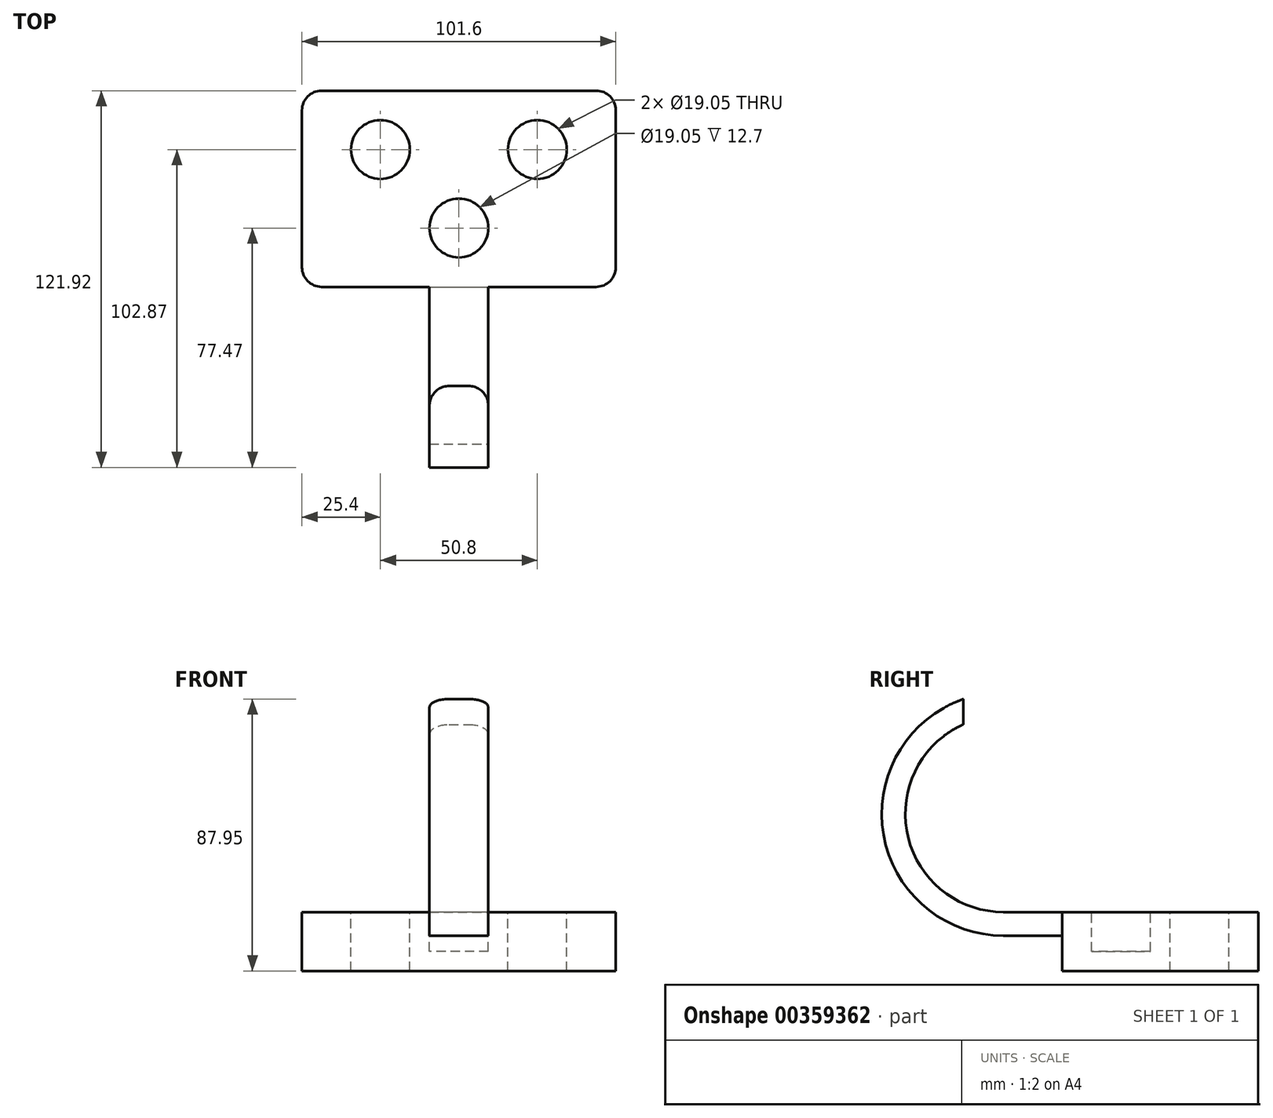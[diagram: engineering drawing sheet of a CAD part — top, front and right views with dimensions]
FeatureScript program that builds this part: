
annotation { "Feature Type Name" : "Feature", "Feature Type Description" : "" }
export const myFeature = defineFeature(function(context is Context, id is Id, definition is map)
    precondition{}
    {
        {
            var Q0;
            Q0=qCreatedBy(makeId("Top.planeOp"),FACE);
            var sketch = newSketch(context, id + "F0", { "sketchPlane" : qUnion([Q0])});
            skLineSegment(sketch, "E0", {"start": v(-50.8, 31.75) * mm, "end": v(-50.8, -31.75) * mm});
            skLineSegment(sketch, "E1", {"start": v(-50.8, -31.75) * mm, "end": v(50.8, -31.75) * mm});
            skLineSegment(sketch, "E2", {"start": v(50.8, -31.75) * mm, "end": v(50.8, 31.75) * mm});
            skLineSegment(sketch, "E3", {"start": v(50.8, 31.75) * mm, "end": v(-50.8, 31.75) * mm});
            skLineSegment(sketch, "E4", {"start": v(-50.8, 0) * mm, "end": v(50.8, 0) * mm});
            skLineSegment(sketch, "E5", {"start": v(0, 31.75) * mm, "end": v(0, -31.75) * mm});
            skCircle(sketch, "E6", {"center": v(-25.4, 12.7) * mm, "radius": 9.53 * mm});
            skCircle(sketch, "E7", {"center": v(25.4, 12.7) * mm, "radius": 9.53 * mm});
            skCircle(sketch, "E8", {"center": v(0, -12.7) * mm, "radius": 9.53 * mm});
            skLineSegment(sketch, "E9", {"start": v(-9.52, -31.75) * mm, "end": v(-9.52, -50.8) * mm});
            skLineSegment(sketch, "E10", {"start": v(-9.52, -50.8) * mm, "end": v(9.53, -50.8) * mm});
            skLineSegment(sketch, "E11", {"start": v(9.53, -50.8) * mm, "end": v(9.53, -31.75) * mm});
            skSolve(sketch);
        }
        {
            var Q0;
            {var subQ3=sQuery(id+"F0.wireOp",EDGE,"E5");var subQ5=sQuery(id+"F0.wireOp",EDGE,"E1");var subQ8=makeQuery(id+"F0.imprint","INTERSECT",VERTEX,{"derivedFrom":[subQ5,subQ3]});Q0=makeQuery(id+"F0.imprint","IMPRINT",FACE,{"disambiguationData":[TD([[makeQuery(id+"F0.imprint","IMPRINT",EDGE,{"disambiguationData":[TD([[subQ8,-1.0]])],"derivedFrom":subQ5}),1.0]])]});}
            var Q1;
            {var subQ0=sQuery(id+"F0.wireOp",EDGE,"E8");var subQ1=sQuery(id+"F0.wireOp",EDGE,"E5");var subQ2=makeQuery(id+"F0.imprint","INTERSECT",VERTEX,{"disambiguationData":[OD(0.0)],"derivedFrom":[subQ1,subQ0]});Q1=makeQuery(id+"F0.imprint","IMPRINT",FACE,{"disambiguationData":[TD([[makeQuery(id+"F0.imprint","IMPRINT",EDGE,{"disambiguationData":[TD([[subQ2,-1.0]])],"derivedFrom":subQ1}),-1.0]])]});}
            var Q2;
            {var subQ1=sQuery(id+"F0.wireOp",EDGE,"E0");var subQ5=sQuery(id+"F0.wireOp",EDGE,"E1");var subQ8=makeQuery(id+"F0.imprint","INTERSECT",VERTEX,{"derivedFrom":[subQ1,subQ5]});Q2=makeQuery(id+"F0.imprint","IMPRINT",FACE,{"disambiguationData":[TD([[makeQuery(id+"F0.imprint","IMPRINT",EDGE,{"disambiguationData":[TD([[subQ8,1.0]])],"derivedFrom":subQ1}),1.0]])]});}
            var Q3;
            {var subQ0=sQuery(id+"F0.wireOp",EDGE,"E8");var subQ1=sQuery(id+"F0.wireOp",EDGE,"E5");var subQ2=makeQuery(id+"F0.imprint","INTERSECT",VERTEX,{"disambiguationData":[OD(0.0)],"derivedFrom":[subQ1,subQ0]});Q3=makeQuery(id+"F0.imprint","IMPRINT",FACE,{"disambiguationData":[TD([[makeQuery(id+"F0.imprint","IMPRINT",EDGE,{"disambiguationData":[TD([[subQ2,-1.0]])],"derivedFrom":subQ1}),1.0]])]});}
            var Q4;
            Q4=makeQuery(id+"F0.imprint","IMPRINT",FACE,{"disambiguationData":[TD([[makeQuery(id+"F0.imprint","IMPRINT",EDGE,{"derivedFrom":sQuery(id+"F0.wireOp",EDGE,"E6")}),1.0]])]});
            var Q5;
            Q5=makeQuery(id+"F0.imprint","IMPRINT",FACE,{"disambiguationData":[TD([[makeQuery(id+"F0.imprint","IMPRINT",EDGE,{"derivedFrom":sQuery(id+"F0.wireOp",EDGE,"E6")}),-1.0]])]});
            var Q6;
            Q6=makeQuery(id+"F0.imprint","IMPRINT",FACE,{"disambiguationData":[TD([[makeQuery(id+"F0.imprint","IMPRINT",EDGE,{"derivedFrom":sQuery(id+"F0.wireOp",EDGE,"E7")}),-1.0]])]});
            var Q7;
            Q7=makeQuery(id+"F0.imprint","IMPRINT",FACE,{"disambiguationData":[TD([[makeQuery(id+"F0.imprint","IMPRINT",EDGE,{"derivedFrom":sQuery(id+"F0.wireOp",EDGE,"E7")}),1.0]])]});
            extrude(context, id + "F1", {"entities" : qUnion([Q0, Q1, Q2, Q3, Q4, Q5, Q6, Q7]), "oppositeDirection" : true, "depth" : 19.05 * mm});
        }
        {
            var Q0;
            {var subQ0=sQuery(id+"F0.wireOp",EDGE,"E9");Q0=makeQuery(id+"F0.imprint","IMPRINT",FACE,{"disambiguationData":[TD([[makeQuery(id+"F0.imprint","IMPRINT",EDGE,{"derivedFrom":subQ0}),1.0]])]});}
            extrude(context, id + "F2", {"entities" : qUnion([Q0]), "operationType" : NewBodyOperationType.ADD, "oppositeDirection" : true, "depth" : 7.62 * mm});
        }
        {
            var Q0;
            Q0=makeQuery(id+"F0.imprint","IMPRINT",FACE,{"disambiguationData":[TD([[makeQuery(id+"F0.imprint","IMPRINT",EDGE,{"derivedFrom":sQuery(id+"F0.wireOp",EDGE,"E6")}),1.0]])]});
            extrude(context, id + "F3", {"entities" : qUnion([Q0]), "operationType" : NewBodyOperationType.REMOVE, "endBound" : BoundingType.THROUGH_ALL, "oppositeDirection" : true, "depth" : 25.4 * mm});
        }
        {
            var Q0;
            {var subQ0=sQuery(id+"F0.wireOp",EDGE,"E8");var subQ1=sQuery(id+"F0.wireOp",EDGE,"E5");var subQ2=makeQuery(id+"F0.imprint","INTERSECT",VERTEX,{"disambiguationData":[OD(0.0)],"derivedFrom":[subQ1,subQ0]});Q0=makeQuery(id+"F0.imprint","IMPRINT",FACE,{"disambiguationData":[TD([[makeQuery(id+"F0.imprint","IMPRINT",EDGE,{"disambiguationData":[TD([[subQ2,-1.0]])],"derivedFrom":subQ1}),-1.0]])]});}
            var Q1;
            {var subQ0=sQuery(id+"F0.wireOp",EDGE,"E8");var subQ1=sQuery(id+"F0.wireOp",EDGE,"E5");var subQ2=makeQuery(id+"F0.imprint","INTERSECT",VERTEX,{"disambiguationData":[OD(0.0)],"derivedFrom":[subQ1,subQ0]});Q1=makeQuery(id+"F0.imprint","IMPRINT",FACE,{"disambiguationData":[TD([[makeQuery(id+"F0.imprint","IMPRINT",EDGE,{"disambiguationData":[TD([[subQ2,-1.0]])],"derivedFrom":subQ1}),1.0]])]});}
            extrude(context, id + "F4", {"entities" : qUnion([Q0, Q1]), "operationType" : NewBodyOperationType.REMOVE, "oppositeDirection" : true, "depth" : 12.7 * mm});
        }
        {
            var Q0;
            Q0=makeQuery(id+"F1.opExtrude","SWEPT_EDGE",EDGE,{"disambiguationData":[OSD([sQuery(id+"F0.wireOp",EDGE,"E0"),sQuery(id+"F0.wireOp",EDGE,"E3")])]});
            var Q1;
            Q1=makeQuery(id+"F1.opExtrude","SWEPT_EDGE",EDGE,{"disambiguationData":[OSD([sQuery(id+"F0.wireOp",EDGE,"E0"),sQuery(id+"F0.wireOp",EDGE,"E1")])]});
            var Q2;
            Q2=makeQuery(id+"F1.opExtrude","SWEPT_EDGE",EDGE,{"disambiguationData":[OSD([sQuery(id+"F0.wireOp",EDGE,"E2"),sQuery(id+"F0.wireOp",EDGE,"E3")])]});
            var Q3;
            Q3=makeQuery(id+"F1.opExtrude","SWEPT_EDGE",EDGE,{"disambiguationData":[OSD([sQuery(id+"F0.wireOp",EDGE,"E1"),sQuery(id+"F0.wireOp",EDGE,"E2")])]});
            fillet(context, id + "F5", {"entities" : qUnion([Q0, Q1, Q2, Q3]), "radius" : 6.35 * mm, "tangentPropagation" : true, "allowEdgeOverflow" : false});
        }
        {
            var Q0;
            Q0=makeQuery(id+"F2.opExtrude","SWEPT_FACE",FACE,{"disambiguationData":[OSD([sQuery(id+"F0.wireOp",EDGE,"E11")])]});
            var sketch = newSketch(context, id + "F6", { "sketchPlane" : qUnion([Q0])});
            skLineSegment(sketch, "E12.0.0", {"start": v(-31.75, 0) * mm, "end": v(-50.8, 0) * mm});
            skLineSegment(sketch, "E12.0.1", {"start": v(-50.8, 0) * mm, "end": v(-50.8, -7.62) * mm});
            skLineSegment(sketch, "E12.0.2", {"start": v(-50.8, -7.62) * mm, "end": v(-31.75, -7.62) * mm});
            skLineSegment(sketch, "E12.0.3", {"start": v(-31.75, -7.62) * mm, "end": v(-31.75, 0) * mm});
            skArc(sketch, "E13", {"start": v(-50.8, -7.62) * mm, "mid": v(-89.61, 25.14) * mm, "end": v(-63.83, 68.9) * mm});
            skLineSegment(sketch, "E14", {"start": v(-63.83, 68.9) * mm, "end": v(-63.83, 60.7) * mm});
            skLineSegment(sketch, "E15", {"start": v(-31.75, -7.62) * mm, "end": v(-31.75, 116.77) * mm});
            skPoint(sketch, "E15.endSnap0", {"position": v(-31.75, -3.81) * mm});
            skArc(sketch, "E16", {"start": v(-50.8, 0) * mm, "mid": v(-81.84, 25.09) * mm, "end": v(-63.83, 60.7) * mm});
            skSolve(sketch);
        }
        {
            var Q0;
            Q0=makeQuery(id+"F6.imprint","IMPRINT",FACE,{"disambiguationData":[TD([[makeQuery(id+"F6.imprint","IMPRINT",EDGE,{"derivedFrom":sQuery(id+"F6.wireOp",EDGE,"E12.0.1")}),1.0]])]});
            extrude(context, id + "F7", {"entities" : qUnion([Q0]), "operationType" : NewBodyOperationType.ADD, "oppositeDirection" : true, "depth" : 19.05 * mm});
        }
        {
            var Q0;
            Q0=makeQuery(id+"F7.opExtrude","CAP_EDGE",EDGE,{"disambiguationData":[OSD([sQuery(id+"F6.wireOp",EDGE,"E14")])],"isStart":true});
            var Q1;
            Q1=makeQuery(id+"F7.opExtrude","CAP_EDGE",EDGE,{"disambiguationData":[OSD([sQuery(id+"F6.wireOp",EDGE,"E14")])],"isStart":false});
            fillet(context, id + "F8", {"entities" : qUnion([Q0, Q1]), "radius" : 6.35 * mm, "tangentPropagation" : true, "allowEdgeOverflow" : false});
        }
        {
            var Q0;
            Q0=makeQuery(id+"F0.imprint","IMPRINT",FACE,{"disambiguationData":[TD([[makeQuery(id+"F0.imprint","IMPRINT",EDGE,{"derivedFrom":sQuery(id+"F0.wireOp",EDGE,"E7")}),1.0]])]});
            extrude(context, id + "F9", {"entities" : qUnion([Q0]), "operationType" : NewBodyOperationType.REMOVE, "oppositeDirection" : true, "depth" : 25.4 * mm});
        }
    });
